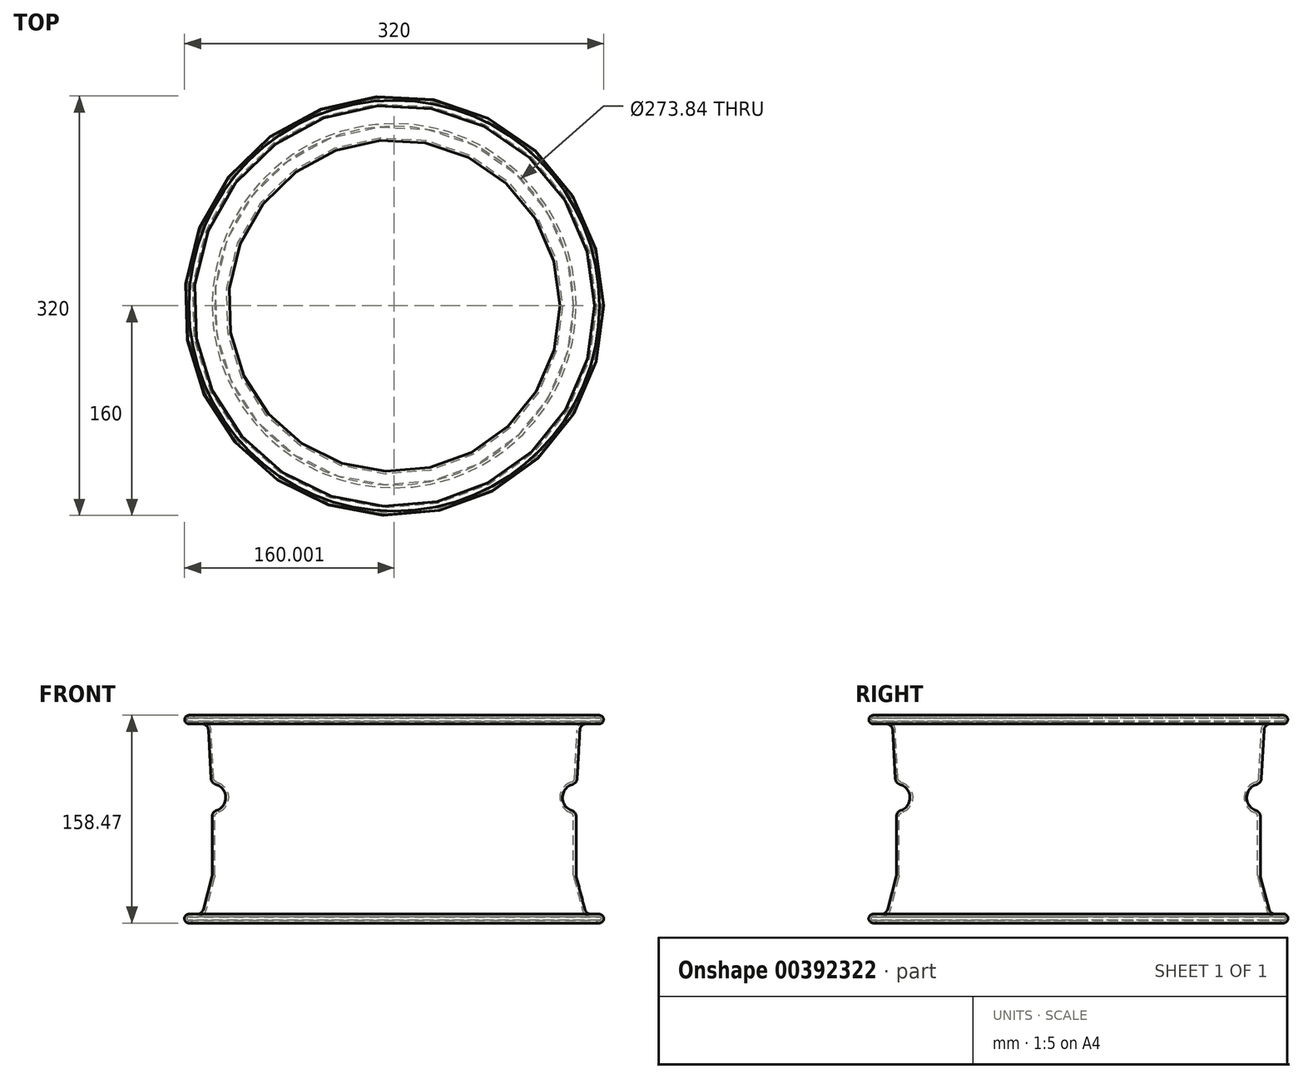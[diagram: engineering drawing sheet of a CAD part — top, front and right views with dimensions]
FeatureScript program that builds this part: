
annotation { "Feature Type Name" : "Feature", "Feature Type Description" : "" }
export const myFeature = defineFeature(function(context is Context, id is Id, definition is map)
    precondition{}
    {
        {
            var Q0;
            Q0=qCreatedBy(makeId("Front.planeOp"),FACE);
            var sketch = newSketch(context, id + "F0", { "sketchPlane" : qUnion([Q0])});
            skLineSegment(sketch, "E0", {"start": v(-125.97, -19.05) * mm, "end": v(-119.82, -19.05) * mm});
            skLineSegment(sketch, "E1", {"start": v(-114.98, -15.33) * mm, "end": v(-108.46, 9.32) * mm});
            skLineSegment(sketch, "E2", {"start": v(-108.3, 10.6) * mm, "end": v(-108.3, 55.33) * mm});
            skLineSegment(sketch, "E3", {"start": v(-109.09, 84.42) * mm, "end": v(-111.12, 121.4) * mm});
            skLineSegment(sketch, "E4", {"start": v(-126.12, 132.63) * mm, "end": v(-123.42, 132.63) * mm});
            skLineSegment(sketch, "E5", {"start": v(-125.97, -25.84) * mm, "end": v(-124.84, -25.84) * mm});
            skArc(sketch, "E6", {"start": v(-125.97, -25.84) * mm, "mid": v(-129.37, -22.44) * mm, "end": v(-125.97, -19.05) * mm});
            skLineSegment(sketch, "E7", {"start": v(-125.97, 126.13) * mm, "end": v(-116.12, 126.13) * mm});
            skArc(sketch, "E8", {"start": v(-125.97, 126.13) * mm, "mid": v(-129.22, 129.3) * mm, "end": v(-126.12, 132.63) * mm});
            skArc(sketch, "E9", {"start": v(-105.46, 79.88) * mm, "mid": v(-97.9, 70.17) * mm, "end": v(-104.91, 60.06) * mm});
            skPoint(sketch, "E10.visualSharp", {"position": v(-111.38, 126.13) * mm});
            skArc(sketch, "E10.filletArc", {"start": v(-111.12, 121.4) * mm, "mid": v(-112.68, 124.76) * mm, "end": v(-116.12, 126.13) * mm});
            skArc(sketch, "E11.filletArc", {"start": v(-109.09, 84.42) * mm, "mid": v(-108, 81.57) * mm, "end": v(-105.46, 79.88) * mm});
            skPoint(sketch, "E12.visualSharp", {"position": v(-108.3, 59.5) * mm});
            skArc(sketch, "E12.filletArc", {"start": v(-104.91, 60.06) * mm, "mid": v(-107.36, 58.24) * mm, "end": v(-108.3, 55.33) * mm});
            skPoint(sketch, "E13.visualSharp", {"position": v(-108.3, 9.95) * mm});
            skArc(sketch, "E13.filletArc", {"start": v(-108.46, 9.32) * mm, "mid": v(-108.33, 9.96) * mm, "end": v(-108.3, 10.6) * mm});
            skPoint(sketch, "E14.visualSharp", {"position": v(-115.97, -19.05) * mm});
            skArc(sketch, "E14.filletArc", {"start": v(-119.82, -19.05) * mm, "mid": v(-116.77, -18) * mm, "end": v(-114.98, -15.33) * mm});
            skLineSegment(sketch, "E15.0", {"start": v(30.63, 137.95) * mm, "end": v(30.63, -34.23) * mm});
            skLineSegment(sketch, "E16.0", {"start": v(190.63, 137.95) * mm, "end": v(190.63, -34.23) * mm, "construction": true});
            skLineSegment(sketch, "E17.0", {"start": v(-126.22, 128.13) * mm, "end": v(-116.12, 128.13) * mm});
            skArc(sketch, "E18.0", {"start": v(-109.12, 121.49) * mm, "mid": v(-111.3, 126.2) * mm, "end": v(-116.12, 128.13) * mm});
            skLineSegment(sketch, "E19.0", {"start": v(-123.42, 132.63) * mm, "end": v(-123.42, 132.63) * mm});
            skLineSegment(sketch, "E20.0", {"start": v(-107.1, 84.52) * mm, "end": v(-109.12, 121.5) * mm});
            skArc(sketch, "E21.0", {"start": v(-104.91, 81.8) * mm, "mid": v(-97.47, 75.89) * mm, "end": v(-96.4, 66.45) * mm});
            skArc(sketch, "E22", {"start": v(-104.91, 81.8) * mm, "mid": v(-106.44, 82.81) * mm, "end": v(-107.1, 84.52) * mm});
            skLineSegment(sketch, "E23.0", {"start": v(-106.3, 10.6) * mm, "end": v(-106.3, 55.34) * mm});
            skLineSegment(sketch, "E24.0", {"start": v(-126.1, -21.05) * mm, "end": v(-119.82, -21.05) * mm});
            skArc(sketch, "E25.0", {"start": v(-119.82, -21.05) * mm, "mid": v(-115.55, -19.6) * mm, "end": v(-113.05, -15.84) * mm});
            skLineSegment(sketch, "E26.0", {"start": v(-113.05, -15.84) * mm, "end": v(-106.52, 8.81) * mm});
            skArc(sketch, "E27", {"start": v(-106.3, 10.6) * mm, "mid": v(-106.35, 9.7) * mm, "end": v(-106.52, 8.81) * mm});
            skArc(sketch, "E28", {"start": v(-104.27, 58.18) * mm, "mid": v(-105.73, 57.09) * mm, "end": v(-106.3, 55.34) * mm});
            skArc(sketch, "E29", {"start": v(-96.4, 66.45) * mm, "mid": v(-99.33, 61.36) * mm, "end": v(-104.27, 58.18) * mm});
            skLineSegment(sketch, "E30", {"start": v(-129.22, 132.63) * mm, "end": v(-129.37, -25) * mm, "construction": true});
            skArc(sketch, "E31", {"start": v(-123.42, 130.63) * mm, "mid": v(-122.42, 131.63) * mm, "end": v(-123.42, 132.63) * mm});
            skLineSegment(sketch, "E32", {"start": v(-123.42, 130.63) * mm, "end": v(-126.22, 130.63) * mm});
            skArc(sketch, "E33", {"start": v(-126.22, 130.63) * mm, "mid": v(-127.46, 129.38) * mm, "end": v(-126.22, 128.13) * mm});
            skArc(sketch, "E34", {"start": v(-124.84, -25.84) * mm, "mid": v(-123.84, -24.84) * mm, "end": v(-124.84, -23.84) * mm});
            skLineSegment(sketch, "E35", {"start": v(-126.1, -23.84) * mm, "end": v(-124.84, -23.84) * mm});
            skArc(sketch, "E36", {"start": v(-126.1, -21.05) * mm, "mid": v(-127.5, -22.44) * mm, "end": v(-126.1, -23.84) * mm});
            skSolve(sketch);
        }
        {
            var Q0;
            Q0=makeQuery(id+"F0.imprint","IMPRINT",FACE,{"disambiguationData":[TD([[makeQuery(id+"F0.imprint","IMPRINT",EDGE,{"derivedFrom":sQuery(id+"F0.wireOp",EDGE,"E0")}),-1.0]])]});
            var Q1;
            Q1=sQuery(id+"F0.wireOp",EDGE,"E26.0");
            var Q2;
            Q2=sQuery(id+"F0.wireOp",EDGE,"E1");
            var Q3;
            Q3=sQuery(id+"F0.wireOp",EDGE,"E21.0");
            var Q4;
            Q4=sQuery(id+"F0.wireOp",EDGE,"E3");
            var Q5;
            Q5=sQuery(id+"F0.wireOp",EDGE,"E2");
            var Q6;
            Q6=sQuery(id+"F0.wireOp",EDGE,"9226ba75-6c61-455b-819a-41e9fab7ad21.0");
            var Q7;
            Q7=sQuery(id+"F0.wireOp",EDGE,"ZDSL2yBL-a5dj-NfuI-e1ZX-pN1Fczb499Jl");
            var Q8;
            Q8=sQuery(id+"F0.wireOp",EDGE,"E9");
            var Q9;
            Q9=sQuery(id+"F0.wireOp",EDGE,"E20.0");
            var Q10;
            Q10=sQuery(id+"F0.wireOp",EDGE,"E23.0");
            var Q11;
            Q11=sQuery(id+"F0.wireOp",EDGE,"E18.0");
            var Q12;
            Q12=sQuery(id+"F0.wireOp",EDGE,"E12.filletArc");
            var Q13;
            Q13=sQuery(id+"F0.wireOp",EDGE,"E11.filletArc");
            var Q14;
            Q14=sQuery(id+"F0.wireOp",EDGE,"E28");
            var Q15;
            Q15=sQuery(id+"F0.wireOp",EDGE,"E29");
            var Q16;
            Q16=sQuery(id+"F0.wireOp",EDGE,"E10.filletArc");
            var Q17;
            Q17=sQuery(id+"F0.wireOp",EDGE,"E17.0");
            var Q18;
            Q18=sQuery(id+"F0.wireOp",EDGE,"E24.0");
            var Q19;
            Q19=sQuery(id+"F0.wireOp",EDGE,"E0");
            var Q20;
            Q20=sQuery(id+"F0.wireOp",EDGE,"6acfbd19-7370-434e-ac6c-36c463c4ff00");
            var Q21;
            Q21=sQuery(id+"F0.wireOp",EDGE,"E6");
            var Q22;
            Q22=sQuery(id+"F0.wireOp",EDGE,"E7");
            var Q23;
            Q23=sQuery(id+"F0.wireOp",EDGE,"E25.0");
            var Q24;
            Q24=sQuery(id+"F0.wireOp",EDGE,"E14.filletArc");
            var Q25;
            Q25=sQuery(id+"F0.wireOp",EDGE,"E22");
            var Q26;
            Q26=sQuery(id+"F0.wireOp",EDGE,"f06582b2-a28b-43a5-8e16-6c8bdb3ea228.filletArc");
            var Q27;
            Q27=sQuery(id+"F0.wireOp",EDGE,"c2f34cc3-9568-4277-b26f-fe3e7d1ce806.filletArc");
            var Q28;
            Q28=sQuery(id+"F0.wireOp",EDGE,"725d37fc-7183-43ab-a264-012caf33fc64");
            var Q29;
            Q29=sQuery(id+"F0.wireOp",EDGE,"E27");
            var Q30;
            Q30=sQuery(id+"F0.wireOp",EDGE,"E8");
            var Q31;
            Q31=sQuery(id+"F0.wireOp",EDGE,"97e7ff8c-38f7-4746-9ef3-44828bc2ad1b");
            var Q32;
            Q32=sQuery(id+"F0.wireOp",EDGE,"E19.0");
            var Q33;
            Q33=sQuery(id+"F0.wireOp",EDGE,"E13.filletArc");
            var Q34;
            Q34=sQuery(id+"F0.wireOp",EDGE,"E4");
            var Q35;
            Q35=sQuery(id+"F0.wireOp",EDGE,"7761872b-eeeb-4fed-89b4-930bdc33babb");
            var Q36;
            Q36=sQuery(id+"F0.wireOp",EDGE,"E5");
            var Q37;
            Q37=sQuery(id+"F0.wireOp",EDGE,"5f529684-0211-42f7-9eb2-275631dadb8d");
            var Q38;
            Q38=sQuery(id+"F0.wireOp",EDGE,"0ad6b574-2588-4e96-8314-be45ab141777.0");
            var Q39;
            Q39=sQuery(id+"F0.wireOp",EDGE,"E15.0");
            revolve(context, id + "F1", {"entities" : qUnion([Q0]), "surfaceEntities" : qUnion([Q1, Q2, Q3, Q4, Q5, Q6, Q7, Q8, Q9, Q10, Q11, Q12, Q13, Q14, Q15, Q16, Q17, Q18, Q19, Q20, Q21, Q22, Q23, Q24, Q25, Q26, Q27, Q28, Q29, Q30, Q31, Q32, Q33, Q34, Q35, Q36, Q37, Q38]), "axis" : qUnion([Q39]), "revolveType" : RevolveType.FULL});
        }
    });
